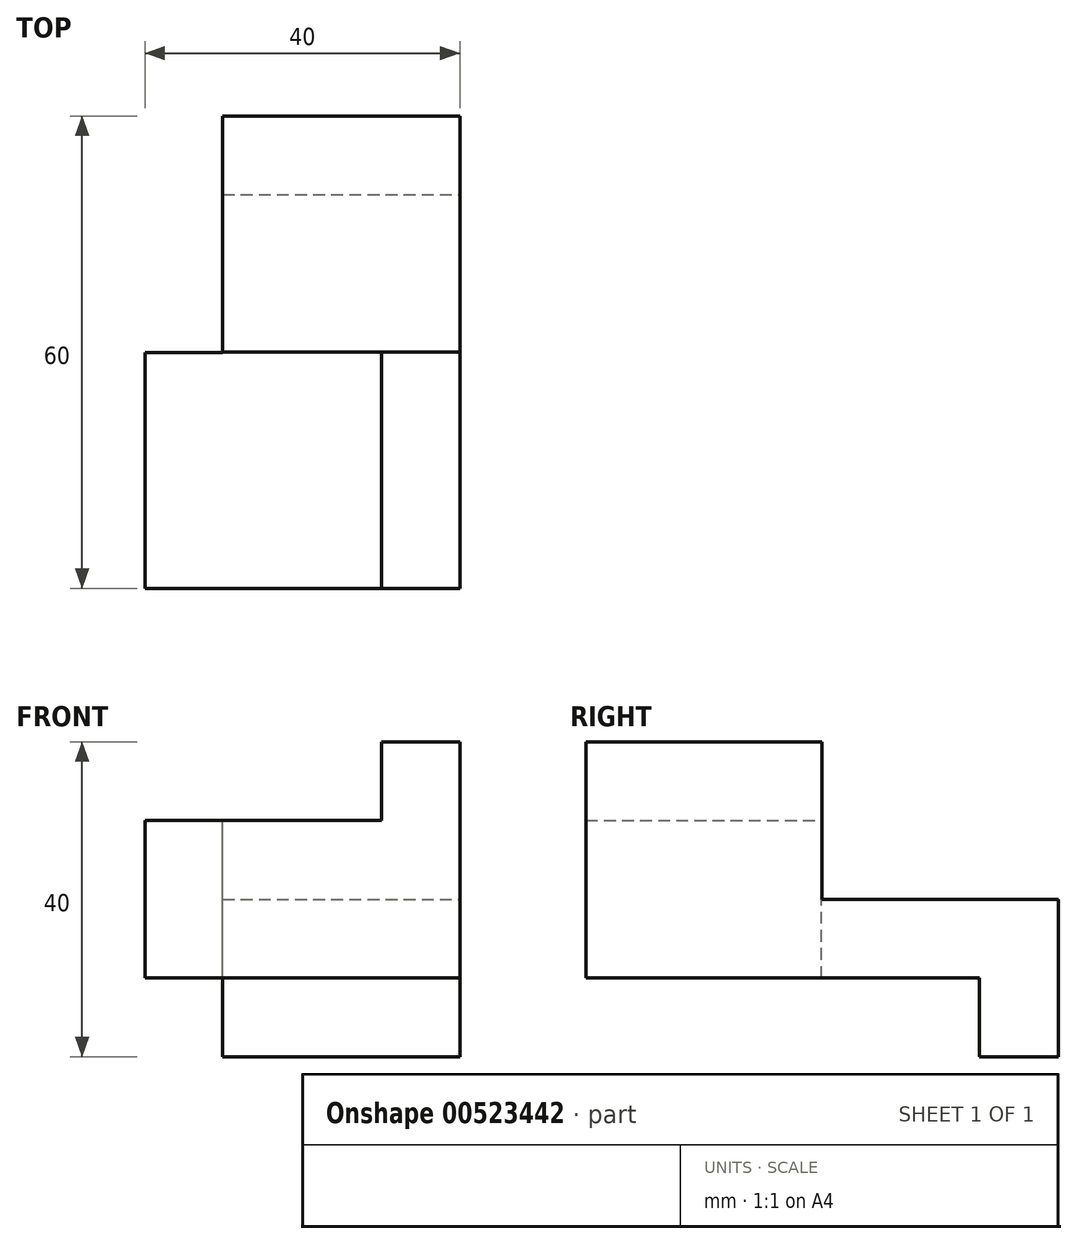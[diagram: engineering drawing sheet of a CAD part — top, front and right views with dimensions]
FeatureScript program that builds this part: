
annotation { "Feature Type Name" : "Feature", "Feature Type Description" : "" }
export const myFeature = defineFeature(function(context is Context, id is Id, definition is map)
    precondition{}
    {
        {
            var Q0;
            Q0=qCreatedBy(makeId("Front.planeOp"),FACE);
            var sketch = newSketch(context, id + "F0", { "sketchPlane" : qUnion([Q0])});
            skLineSegment(sketch, "E0.bottom", {"start": v(0, 0) * mm, "end": v(40, 0) * mm});
            skLineSegment(sketch, "E0.top", {"start": v(0, 40) * mm, "end": v(40, 40) * mm});
            skLineSegment(sketch, "E0.left", {"start": v(0, 0) * mm, "end": v(0, 40) * mm});
            skLineSegment(sketch, "E0.right", {"start": v(40, 0) * mm, "end": v(40, 40) * mm});
            skSolve(sketch);
        }
        {
            var Q0;
            Q0 = qSketchRegion(id + "F0", true);
            extrude(context, id + "F1", {"entities" : qUnion([Q0]), "depth" : 60 * mm, "offsetDistance" : 25.4 * mm});
        }
        {
            var Q0;
            Q0=makeQuery(id+"F1.opExtrude","CAP_FACE",FACE,{"disambiguationData":[OSD([sQuery(id+"F0.wireOp",EDGE,"E0.bottom"),sQuery(id+"F0.wireOp",EDGE,"E0.top"),sQuery(id+"F0.wireOp",EDGE,"E0.left"),sQuery(id+"F0.wireOp",EDGE,"E0.right")])],"isStart":false});
            var sketch = newSketch(context, id + "F2", { "sketchPlane" : qUnion([Q0])});
            skLineSegment(sketch, "E1.bottom", {"start": v(0, 0) * mm, "end": v(10, 0) * mm});
            skLineSegment(sketch, "E1.top", {"start": v(0, 10) * mm, "end": v(10, 10) * mm});
            skLineSegment(sketch, "E1.left", {"start": v(0, 0) * mm, "end": v(0, 10) * mm});
            skLineSegment(sketch, "E1.right", {"start": v(10, 0) * mm, "end": v(10, 10) * mm});
            skSolve(sketch);
        }
        {
            var Q0;
            Q0=makeQuery(id+"F2.imprint","IMPRINT",FACE,{"disambiguationData":[TD([[makeQuery(id+"F2.imprint","IMPRINT",EDGE,{"derivedFrom":sQuery(id+"F2.wireOp",EDGE,"E1.bottom")}),1.0]])]});
            extrude(context, id + "F3", {"entities" : qUnion([Q0]), "operationType" : NewBodyOperationType.REMOVE, "oppositeDirection" : true, "depth" : 50 * mm, "offsetDistance" : 25.4 * mm});
        }
        {
            var Q0;
            Q0=makeQuery(id+"F1.opExtrude","SWEPT_FACE",FACE,{"disambiguationData":[OSD([sQuery(id+"F0.wireOp",EDGE,"E0.top")])]});
            var sketch = newSketch(context, id + "F4", { "sketchPlane" : qUnion([Q0])});
            skLineSegment(sketch, "E2.bottom", {"start": v(0, 0) * mm, "end": v(9.86, 0) * mm});
            skLineSegment(sketch, "E2.top", {"start": v(0, -30.08) * mm, "end": v(9.86, -30.08) * mm});
            skLineSegment(sketch, "E2.left", {"start": v(0, 0) * mm, "end": v(0, -30.08) * mm});
            skLineSegment(sketch, "E2.right", {"start": v(9.86, 0) * mm, "end": v(9.86, -30.08) * mm});
            skSolve(sketch);
        }
        {
            var Q0;
            Q0 = qSketchRegion(id + "F4", true);
            extrude(context, id + "F5", {"entities" : qUnion([Q0]), "operationType" : NewBodyOperationType.REMOVE, "oppositeDirection" : true, "depth" : 20 * mm, "offsetDistance" : 25 * mm});
        }
        {
            var Q0;
            Q0=makeQuery(id+"F1.opExtrude","SWEPT_FACE",FACE,{"disambiguationData":[OSD([sQuery(id+"F0.wireOp",EDGE,"E0.top")])]});
            var sketch = newSketch(context, id + "F6", { "sketchPlane" : qUnion([Q0])});
            skLineSegment(sketch, "E3.bottom", {"start": v(0, -60) * mm, "end": v(30.08, -60) * mm});
            skLineSegment(sketch, "E3.top", {"start": v(0, -30.08) * mm, "end": v(30.08, -30.08) * mm});
            skLineSegment(sketch, "E3.left", {"start": v(0, -60) * mm, "end": v(0, -30.08) * mm});
            skLineSegment(sketch, "E3.right", {"start": v(30.08, -60) * mm, "end": v(30.08, -30.08) * mm});
            skSolve(sketch);
        }
        {
            var Q0;
            Q0=makeQuery(id+"F6.imprint","IMPRINT",FACE,{"disambiguationData":[TD([[makeQuery(id+"F6.imprint","IMPRINT",EDGE,{"derivedFrom":sQuery(id+"F6.wireOp",EDGE,"E3.bottom")}),1.0]])]});
            extrude(context, id + "F7", {"entities" : qUnion([Q0]), "operationType" : NewBodyOperationType.REMOVE, "oppositeDirection" : true, "depth" : 10 * mm, "offsetDistance" : 25 * mm});
        }
        {
            var Q0;
            Q0=makeQuery(id+"F3.boolean.opBoolean","COPY",FACE,{"derivedFrom":makeQuery(id+"F3.opExtrude","SWEPT_FACE",FACE,{"disambiguationData":[OSD([sQuery(id+"F2.wireOp",EDGE,"E1.right")])]})});
            extrude(context, id + "F8", {"entities" : qUnion([Q0]), "operationType" : NewBodyOperationType.REMOVE, "endBound" : BoundingType.THROUGH_ALL, "oppositeDirection" : true, "depth" : 25 * mm, "offsetDistance" : 25 * mm});
        }
        {
            var Q0;
            Q0=makeQuery(id+"F5.boolean.opBoolean","COPY",FACE,{"derivedFrom":makeQuery(id+"F5.opExtrude","CAP_FACE",FACE,{"disambiguationData":[OSD([sQuery(id+"F4.wireOp",EDGE,"E2.bottom"),sQuery(id+"F4.wireOp",EDGE,"E2.top"),sQuery(id+"F4.wireOp",EDGE,"E2.left"),sQuery(id+"F4.wireOp",EDGE,"E2.right")])],"isStart":false})});
            extrude(context, id + "F9", {"entities" : qUnion([Q0]), "operationType" : NewBodyOperationType.REMOVE, "endBound" : BoundingType.THROUGH_ALL, "oppositeDirection" : true, "depth" : 25 * mm, "offsetDistance" : 25 * mm});
        }
        {
            var Q0;
            Q0=makeQuery(id+"F1.opExtrude","SWEPT_FACE",FACE,{"disambiguationData":[OSD([sQuery(id+"F0.wireOp",EDGE,"E0.top")])]});
            var sketch = newSketch(context, id + "F10", { "sketchPlane" : qUnion([Q0])});
            skLineSegment(sketch, "E4.bottom", {"start": v(9.86, 0) * mm, "end": v(40, 0) * mm});
            skLineSegment(sketch, "E4.top", {"start": v(9.86, -30) * mm, "end": v(40, -30) * mm});
            skLineSegment(sketch, "E4.left", {"start": v(9.86, 0) * mm, "end": v(9.86, -30) * mm});
            skLineSegment(sketch, "E4.right", {"start": v(40, 0) * mm, "end": v(40, -30) * mm});
            skSolve(sketch);
        }
        {
            var Q0;
            Q0=makeQuery(id+"F10.imprint","IMPRINT",FACE,{"disambiguationData":[TD([[makeQuery(id+"F10.imprint","IMPRINT",EDGE,{"derivedFrom":sQuery(id+"F10.wireOp",EDGE,"E4.bottom")}),-1.0]])]});
            extrude(context, id + "F11", {"entities" : qUnion([Q0]), "operationType" : NewBodyOperationType.REMOVE, "oppositeDirection" : true, "depth" : 20 * mm, "offsetDistance" : 25 * mm});
        }
        {
            var Q0;
            Q0=makeQuery(id+"F7.boolean.opBoolean","COPY",FACE,{"derivedFrom":makeQuery(id+"F7.opExtrude","SWEPT_FACE",FACE,{"disambiguationData":[OSD([sQuery(id+"F6.wireOp",EDGE,"E3.top")])]})});
            extrude(context, id + "F12", {"entities" : qUnion([Q0]), "operationType" : NewBodyOperationType.REMOVE, "oppositeDirection" : true, "depth" : 20 * mm, "offsetDistance" : 25 * mm});
        }
    });
